# Revit family: Proxway_Сетевой_IP-контроллер_доступа_PW-400_EU
name_source: partatom
category: Электрооборудование
units: mm (PartAtom-declared; Revit-internal decimal feet)

## family parameters
Всегда вертикально = Нет
На основе рабочей плоскости = Нет
Общий = Да
При загрузке вырезать с полостями = Нет
Размер круглого соединителя = Использовать диаметр
Тип детали = Другая панель
Точка расчета площади = Да

## types (1)
- PW-400 EU mod.23
    =Габариты= = =Габариты=
    ADSK_Единица измерения = шт.
    ADSK_Завод-изготовитель = Proxway
    ADSK_Количество = 1
    ADSK_Марка = PW-400 EU mod.23
    ADSK_Наименование = Сетевой контроллер СКУД в корпусе без блока питания
    ADSK_Обозначение = КД
    ADSK_Раздел спецификации = 2. Центральное оборудование
    ADSK_Размер_Высота = 136 мм
    ADSK_Размер_Глубина = 40 мм
    ADSK_Размер_Ширина = 183 мм
    ADSK_Тип = PW-400 EU mod.23
    ADSK_Ток дежурного режима = 250.000 мА
    ADSK_Ток тревожного режима = 250.000 мА
    URL = https://proxway-ble.ru
    Зона обслуживания_Отступ от прибора = 50 мм
    Отметка по умолчанию = 0 мм
    Текст модели = PW-400 EU mod.23
    УГО_Тип = УГО_СС_Контроллер
